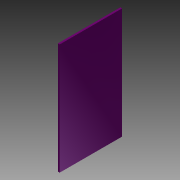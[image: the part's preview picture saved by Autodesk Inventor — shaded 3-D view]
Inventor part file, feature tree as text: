
AUTODESK INVENTOR PART (.ipt)
format: ipt  version: 2015 (Build 190159000, 159)  size: 89,088 bytes
history: native  units: in
note: dims shown in document units (in); Inventor stores cm internally (conversion verified against a paired STEP export)
features: extrude x1, sketch x1
ambient origin geometry x8: Origin, YZ Plane, XZ Plane, XY Plane, X Axis, Y Axis, Z Axis, Center Point
bodies: Solid1 (feature_tree)
feature tree (2):
  extrude  "Extrusion1"  Depth=2.25in
  sketch  "Sketch1"  dims[d0=4.0in d2=2.25in d3=0.0646in d4=0.0in]
